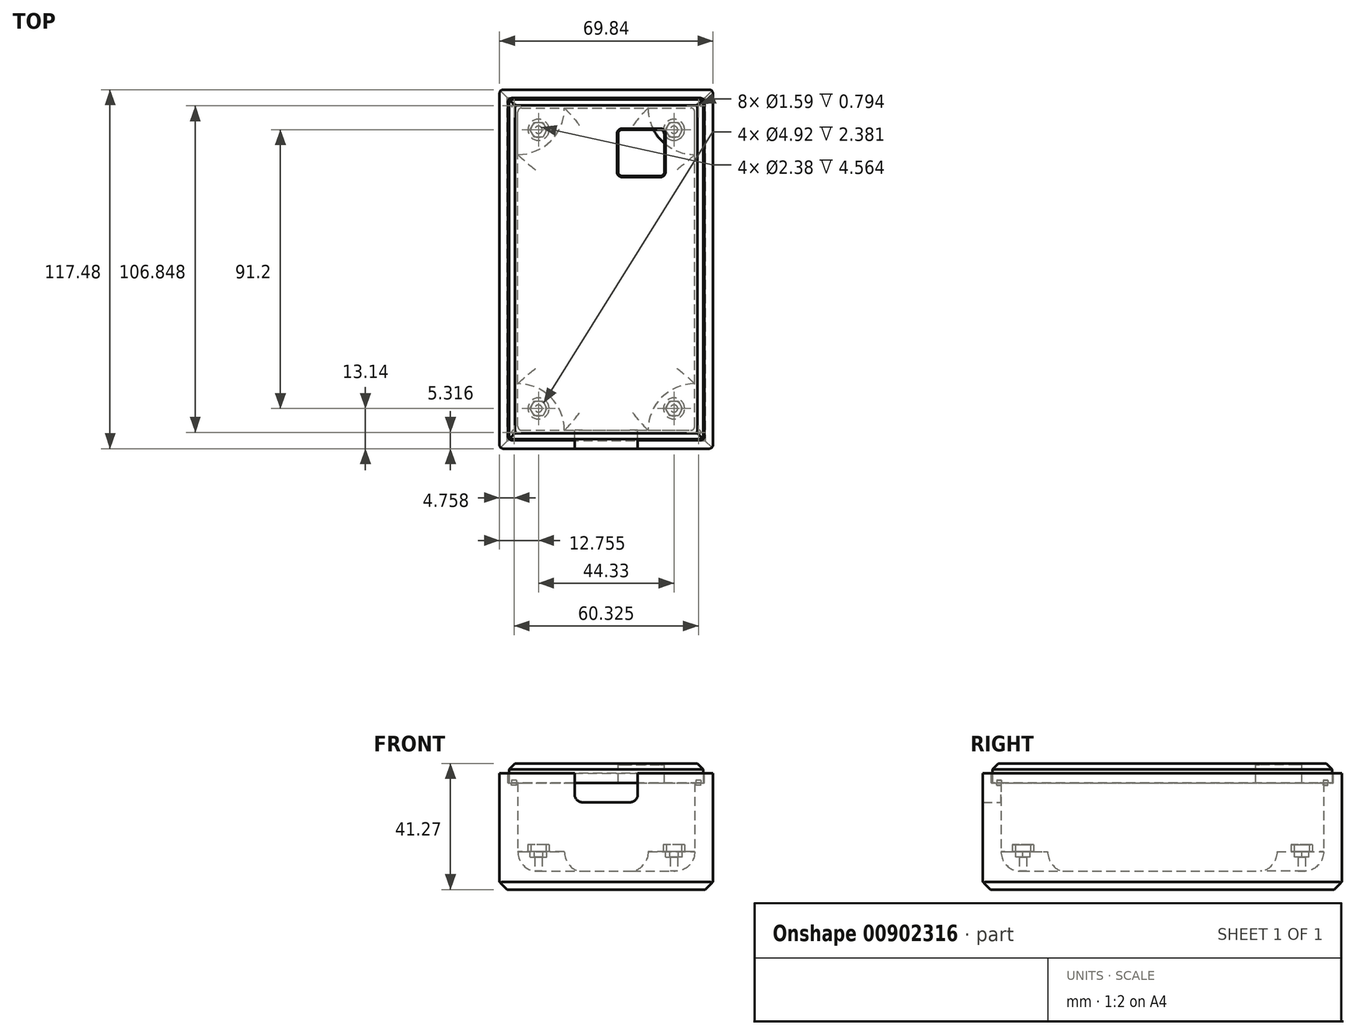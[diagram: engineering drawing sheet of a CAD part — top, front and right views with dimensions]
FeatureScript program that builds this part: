
annotation { "Feature Type Name" : "Feature", "Feature Type Description" : "" }
export const myFeature = defineFeature(function(context is Context, id is Id, definition is map)
    precondition{}
    {
        {
            var Q0;
            Q0=qCreatedBy(makeId("Top.planeOp"),FACE);
            var sketch = newSketch(context, id + "F0", { "sketchPlane" : qUnion([Q0])});
            skLineSegment(sketch, "E0.bottom", {"start": v(-34.92, -58.74) * mm, "end": v(34.93, -58.74) * mm});
            skLineSegment(sketch, "E0.top", {"start": v(-34.93, 58.74) * mm, "end": v(34.92, 58.74) * mm});
            skLineSegment(sketch, "E0.left", {"start": v(-34.92, -58.74) * mm, "end": v(-34.93, 58.74) * mm});
            skLineSegment(sketch, "E0.right", {"start": v(34.93, -58.74) * mm, "end": v(34.92, 58.74) * mm});
            skPoint(sketch, "E0.middle", {"position": v(0, 0) * mm});
            skSolve(sketch);
        }
        {
            var Q0;
            Q0=makeQuery(id+"F0.imprint","IMPRINT",FACE,{"disambiguationData":[TD([[makeQuery(id+"F0.imprint","IMPRINT",EDGE,{"derivedFrom":sQuery(id+"F0.wireOp",EDGE,"E0.bottom")}),1.0]])]});
            extrude(context, id + "F1", {"entities" : qUnion([Q0]), "depth" : 38.1 * mm, "offsetDistance" : 25.4 * mm});
        }
        {
            var Q0;
            Q0=makeQuery(id+"F1.opExtrude","CAP_FACE",FACE,{"disambiguationData":[OSD([sQuery(id+"F0.wireOp",EDGE,"E0.bottom"),sQuery(id+"F0.wireOp",EDGE,"E0.top"),sQuery(id+"F0.wireOp",EDGE,"E0.left"),sQuery(id+"F0.wireOp",EDGE,"E0.right")])],"isStart":false});
            shell(context, id + "F2", {"entities" : qUnion([Q0]), "thickness" : 6 * mm});
        }
        {
            var Q0;
            Q0=makeQuery(id+"F1.opExtrude","CAP_FACE",FACE,{"disambiguationData":[OSD([sQuery(id+"F0.wireOp",EDGE,"E0.bottom"),sQuery(id+"F0.wireOp",EDGE,"E0.top"),sQuery(id+"F0.wireOp",EDGE,"E0.left"),sQuery(id+"F0.wireOp",EDGE,"E0.right")])],"isStart":false});
            cPlane(context, id + "F3", {"entities" : qUnion([Q0]), "cplaneType" : CPlaneType.OFFSET, "offset" : 0 * mm, "oppositeDirection" : true, "width" : 152.4 * mm, "height" : 152.4 * mm});
        }
        {
            var Q0;
            Q0=qCreatedBy(id+"F3.planeOp",FACE);
            var sketch = newSketch(context, id + "F4", { "sketchPlane" : qUnion([Q0])});
            skLineSegment(sketch, "E1.bottom", {"start": v(32.15, -55.96) * mm, "end": v(-32.15, -55.96) * mm});
            skLineSegment(sketch, "E1.top", {"start": v(32.15, 55.96) * mm, "end": v(-32.15, 55.96) * mm});
            skLineSegment(sketch, "E1.left", {"start": v(32.15, -55.96) * mm, "end": v(32.15, 55.96) * mm});
            skLineSegment(sketch, "E1.right", {"start": v(-32.15, -55.96) * mm, "end": v(-32.15, 55.96) * mm});
            skPoint(sketch, "E1.middle", {"position": v(0, 0) * mm});
            skSolve(sketch);
        }
        {
            var Q0;
            Q0 = qSketchRegion(id + "F4", true);
            extrude(context, id + "F5", {"entities" : qUnion([Q0]), "operationType" : NewBodyOperationType.REMOVE, "oppositeDirection" : true, "depth" : 3.17 * mm, "offsetDistance" : 25.4 * mm});
        }
        {
            var Q0;
            Q0=makeQuery(id+"F2.opShell","OFFSET_FACE",FACE,{"disambiguationData":[OSD([sQuery(id+"F0.wireOp",EDGE,"E0.bottom"),sQuery(id+"F0.wireOp",EDGE,"E0.top"),sQuery(id+"F0.wireOp",EDGE,"E0.left"),sQuery(id+"F0.wireOp",EDGE,"E0.right")])]});
            var sketch = newSketch(context, id + "F6", { "sketchPlane" : qUnion([Q0])});
            skArc(sketch, "E2", {"start": v(-13.69, -52.74) * mm, "mid": v(-18.15, -41.96) * mm, "end": v(-28.93, -37.5) * mm});
            skArc(sketch, "E3", {"start": v(-28.93, 37.5) * mm, "mid": v(-18.15, 41.96) * mm, "end": v(-13.69, 52.74) * mm});
            skArc(sketch, "E4", {"start": v(28.93, -37.5) * mm, "mid": v(18.15, -41.96) * mm, "end": v(13.69, -52.74) * mm});
            skArc(sketch, "E5", {"start": v(13.68, 52.74) * mm, "mid": v(18.15, 41.96) * mm, "end": v(28.92, 37.5) * mm});
            skLineSegment(sketch, "E6", {"start": v(-28.93, 0) * mm, "end": v(28.93, 0) * mm, "construction": true});
            skLineSegment(sketch, "E7", {"start": v(0, -52.74) * mm, "end": v(0, 52.74) * mm, "construction": true});
            skCircle(sketch, "E8", {"center": v(-22.16, -45.6) * mm, "radius": 1.2 * mm});
            skCircle(sketch, "E9", {"center": v(22.16, -45.6) * mm, "radius": 1.2 * mm});
            skCircle(sketch, "E10", {"center": v(22.16, 45.6) * mm, "radius": 1.2 * mm});
            skCircle(sketch, "E11", {"center": v(-22.16, 45.6) * mm, "radius": 1.2 * mm});
            skLineSegment(sketch, "E12", {"start": v(-28.93, -37.5) * mm, "end": v(-28.93, -52.74) * mm});
            skLineSegment(sketch, "E13", {"start": v(-13.69, -52.74) * mm, "end": v(-28.93, -52.74) * mm});
            skLineSegment(sketch, "E14", {"start": v(13.69, -52.74) * mm, "end": v(28.93, -52.74) * mm});
            skLineSegment(sketch, "E15", {"start": v(28.93, -52.74) * mm, "end": v(28.93, -37.5) * mm});
            skLineSegment(sketch, "E16", {"start": v(-28.93, 37.5) * mm, "end": v(-28.93, 52.74) * mm});
            skLineSegment(sketch, "E17", {"start": v(-28.93, 52.74) * mm, "end": v(-13.69, 52.74) * mm});
            skLineSegment(sketch, "E18", {"start": v(13.68, 52.74) * mm, "end": v(28.92, 52.74) * mm});
            skLineSegment(sketch, "E19", {"start": v(28.92, 37.5) * mm, "end": v(28.92, 52.74) * mm});
            skSolve(sketch);
        }
        {
            var Q0;
            Q0 = qSketchRegion(id + "F6", true);
            extrude(context, id + "F7", {"entities" : qUnion([Q0]), "operationType" : NewBodyOperationType.ADD, "depth" : 6.35 * mm, "offsetDistance" : 25.4 * mm});
        }
        {
            var Q0;
            Q0=makeQuery(id+"F7.opExtrude","CAP_FACE",FACE,{"disambiguationData":[OSD([sQuery(id+"F6.wireOp",EDGE,"E2"),sQuery(id+"F6.wireOp",EDGE,"E8"),sQuery(id+"F6.wireOp",EDGE,"E12"),sQuery(id+"F6.wireOp",EDGE,"E13")])],"isStart":false});
            cPlane(context, id + "F8", {"entities" : qUnion([Q0]), "cplaneType" : CPlaneType.OFFSET, "offset" : 0 * mm, "width" : 152.4 * mm, "height" : 152.4 * mm});
        }
        {
            var Q0;
            Q0=qCreatedBy(id+"F8.planeOp",FACE);
            var sketch = newSketch(context, id + "F9", { "sketchPlane" : qUnion([Q0])});
            skCircle(sketch, "E20.cCircle", {"center": v(-22.16, -45.6) * mm, "radius": 2.75 * mm, "construction": true});
            skLineSegment(sketch, "E20.0", {"start": v(-19.41, -45.6) * mm, "end": v(-20.79, -47.98) * mm});
            skLineSegment(sketch, "E20.1", {"start": v(-20.79, -47.98) * mm, "end": v(-23.54, -47.98) * mm});
            skLineSegment(sketch, "E20.2", {"start": v(-23.54, -47.98) * mm, "end": v(-24.91, -45.6) * mm});
            skLineSegment(sketch, "E20.3", {"start": v(-24.91, -45.6) * mm, "end": v(-23.54, -43.22) * mm});
            skLineSegment(sketch, "E20.4", {"start": v(-23.54, -43.22) * mm, "end": v(-20.79, -43.22) * mm});
            skLineSegment(sketch, "E20.5", {"start": v(-20.79, -43.22) * mm, "end": v(-19.41, -45.6) * mm});
            skCircle(sketch, "E21.cCircle", {"center": v(22.16, -45.6) * mm, "radius": 2.75 * mm, "construction": true});
            skLineSegment(sketch, "E21.0", {"start": v(23.54, -47.98) * mm, "end": v(20.79, -47.98) * mm});
            skLineSegment(sketch, "E21.1", {"start": v(20.79, -47.98) * mm, "end": v(19.42, -45.6) * mm});
            skLineSegment(sketch, "E21.2", {"start": v(19.41, -45.6) * mm, "end": v(20.8, -43.22) * mm});
            skLineSegment(sketch, "E21.3", {"start": v(20.8, -43.22) * mm, "end": v(23.54, -43.22) * mm});
            skLineSegment(sketch, "E21.4", {"start": v(23.54, -43.22) * mm, "end": v(24.91, -45.6) * mm});
            skLineSegment(sketch, "E21.5", {"start": v(24.92, -45.6) * mm, "end": v(23.54, -47.98) * mm});
            skLineSegment(sketch, "E22", {"start": v(-23.36, -45.6) * mm, "end": v(-20.97, -45.6) * mm, "construction": true});
            skLineSegment(sketch, "E23", {"start": v(22.16, -46.8) * mm, "end": v(22.16, -44.4) * mm, "construction": true});
            skLineSegment(sketch, "E24", {"start": v(22.16, 44.4) * mm, "end": v(22.16, 46.8) * mm, "construction": true});
            skLineSegment(sketch, "E25", {"start": v(-23.36, 45.6) * mm, "end": v(-20.97, 45.6) * mm, "construction": true});
            skCircle(sketch, "E26.cCircle", {"center": v(-22.16, 45.6) * mm, "radius": 2.75 * mm, "construction": true});
            skLineSegment(sketch, "E26.0", {"start": v(-20.79, 47.98) * mm, "end": v(-19.41, 45.6) * mm});
            skLineSegment(sketch, "E26.1", {"start": v(-19.41, 45.6) * mm, "end": v(-20.79, 43.22) * mm});
            skLineSegment(sketch, "E26.2", {"start": v(-20.79, 43.22) * mm, "end": v(-23.54, 43.22) * mm});
            skLineSegment(sketch, "E26.3", {"start": v(-23.54, 43.22) * mm, "end": v(-24.91, 45.6) * mm});
            skLineSegment(sketch, "E26.4", {"start": v(-24.91, 45.6) * mm, "end": v(-23.54, 47.98) * mm});
            skLineSegment(sketch, "E26.5", {"start": v(-23.54, 47.98) * mm, "end": v(-20.79, 47.98) * mm});
            skCircle(sketch, "E27.cCircle", {"center": v(22.16, 45.6) * mm, "radius": 2.75 * mm, "construction": true});
            skLineSegment(sketch, "E27.0", {"start": v(24.91, 45.6) * mm, "end": v(23.54, 43.22) * mm});
            skLineSegment(sketch, "E27.1", {"start": v(23.54, 43.22) * mm, "end": v(20.79, 43.22) * mm});
            skLineSegment(sketch, "E27.2", {"start": v(20.79, 43.22) * mm, "end": v(19.41, 45.6) * mm});
            skLineSegment(sketch, "E27.3", {"start": v(19.41, 45.6) * mm, "end": v(20.79, 47.98) * mm});
            skLineSegment(sketch, "E27.4", {"start": v(20.79, 47.98) * mm, "end": v(23.54, 47.98) * mm});
            skLineSegment(sketch, "E27.5", {"start": v(23.54, 47.98) * mm, "end": v(24.91, 45.6) * mm});
            skSolve(sketch);
        }
        {
            var Q0;
            Q0 = qSketchRegion(id + "F9", true);
            extrude(context, id + "F10", {"entities" : qUnion([Q0]), "operationType" : NewBodyOperationType.REMOVE, "oppositeDirection" : true, "depth" : 1.79 * mm, "offsetDistance" : 25.4 * mm});
        }
        {
            var Q0;
            Q0=makeQuery(id+"F1.opExtrude","CAP_FACE",FACE,{"disambiguationData":[OSD([sQuery(id+"F0.wireOp",EDGE,"E0.bottom"),sQuery(id+"F0.wireOp",EDGE,"E0.top"),sQuery(id+"F0.wireOp",EDGE,"E0.left"),sQuery(id+"F0.wireOp",EDGE,"E0.right")])],"isStart":false});
            var sketch = newSketch(context, id + "F11", { "sketchPlane" : qUnion([Q0])});
            skLineSegment(sketch, "E28.bottom", {"start": v(-10.32, -58.74) * mm, "end": v(10.32, -58.74) * mm});
            skLineSegment(sketch, "E28.top", {"start": v(-10.32, -52.22) * mm, "end": v(10.32, -52.22) * mm});
            skLineSegment(sketch, "E28.left", {"start": v(-10.32, -58.74) * mm, "end": v(-10.32, -52.22) * mm});
            skLineSegment(sketch, "E28.right", {"start": v(10.32, -58.74) * mm, "end": v(10.32, -52.22) * mm});
            skLineSegment(sketch, "E29", {"start": v(0, -58.74) * mm, "end": v(0, 58.74) * mm, "construction": true});
            skSolve(sketch);
        }
        {
            var Q0;
            Q0 = qSketchRegion(id + "F11", true);
            extrude(context, id + "F12", {"entities" : qUnion([Q0]), "operationType" : NewBodyOperationType.REMOVE, "oppositeDirection" : true, "depth" : 9.52 * mm, "offsetDistance" : 25.4 * mm});
        }
        {
            var Q0;
            {var subQ0=sQuery(id+"F0.wireOp",EDGE,"E0.right");var subQ1=sQuery(id+"F0.wireOp",EDGE,"E0.left");var subQ2=sQuery(id+"F0.wireOp",EDGE,"E0.top");var subQ3=sQuery(id+"F0.wireOp",EDGE,"E0.bottom");Q0=makeQuery(id+"F7.boolean.opBoolean","SPLIT",FACE,{"disambiguationData":[TD([makeQuery(id+"F2.opShell","OFFSET_FACE",FACE,{"disambiguationData":[OSD([subQ3])]})])],"derivedFrom":makeQuery(id+"F2.opShell","OFFSET_FACE",FACE,{"disambiguationData":[OSD([subQ3,subQ2,subQ1,subQ0])]})});}
            fillet(context, id + "F13", {"entities" : qUnion([Q0]), "radius" : 6.35 * mm, "tangentPropagation" : true, "allowEdgeOverflow" : false});
        }
        {
            var Q0;
            Q0=makeQuery(id+"F2.opShell","OFFSET_EDGE",EDGE,{"disambiguationData":[OSD([sQuery(id+"F0.wireOp",EDGE,"E0.bottom"),sQuery(id+"F0.wireOp",EDGE,"E0.left")])]});
            var Q1;
            Q1=makeQuery(id+"F2.opShell","OFFSET_EDGE",EDGE,{"disambiguationData":[OSD([sQuery(id+"F0.wireOp",EDGE,"E0.top"),sQuery(id+"F0.wireOp",EDGE,"E0.left")])]});
            var Q2;
            Q2=makeQuery(id+"F2.opShell","OFFSET_EDGE",EDGE,{"disambiguationData":[OSD([sQuery(id+"F0.wireOp",EDGE,"E0.bottom"),sQuery(id+"F0.wireOp",EDGE,"E0.right")])]});
            var Q3;
            Q3=makeQuery(id+"F2.opShell","OFFSET_EDGE",EDGE,{"disambiguationData":[OSD([sQuery(id+"F0.wireOp",EDGE,"E0.top"),sQuery(id+"F0.wireOp",EDGE,"E0.right")])]});
            fillet(context, id + "F14", {"entities" : qUnion([Q0, Q1, Q2, Q3]), "radius" : 1.27 * mm, "tangentPropagation" : true, "allowEdgeOverflow" : false});
        }
        {
            var Q0;
            Q0=makeQuery(id+"F1.opExtrude","CAP_FACE",FACE,{"disambiguationData":[OSD([sQuery(id+"F0.wireOp",EDGE,"E0.bottom"),sQuery(id+"F0.wireOp",EDGE,"E0.top"),sQuery(id+"F0.wireOp",EDGE,"E0.left"),sQuery(id+"F0.wireOp",EDGE,"E0.right")])],"isStart":true});
            chamfer(context, id + "F15", {"entities" : qUnion([Q0]), "width" : 2.54 * mm, "tangentPropagation" : true});
        }
        {
            var Q0;
            Q0=makeQuery(id+"F1.opExtrude","SWEPT_EDGE",EDGE,{"disambiguationData":[OSD([sQuery(id+"F0.wireOp",EDGE,"E0.bottom"),sQuery(id+"F0.wireOp",EDGE,"E0.right")])]});
            var Q1;
            Q1=makeQuery(id+"F1.opExtrude","SWEPT_EDGE",EDGE,{"disambiguationData":[OSD([sQuery(id+"F0.wireOp",EDGE,"E0.bottom"),sQuery(id+"F0.wireOp",EDGE,"E0.left")])]});
            var Q2;
            Q2=makeQuery(id+"F1.opExtrude","SWEPT_EDGE",EDGE,{"disambiguationData":[OSD([sQuery(id+"F0.wireOp",EDGE,"E0.top"),sQuery(id+"F0.wireOp",EDGE,"E0.left")])]});
            var Q3;
            Q3=makeQuery(id+"F1.opExtrude","SWEPT_EDGE",EDGE,{"disambiguationData":[OSD([sQuery(id+"F0.wireOp",EDGE,"E0.top"),sQuery(id+"F0.wireOp",EDGE,"E0.right")])]});
            fillet(context, id + "F16", {"entities" : qUnion([Q0, Q1, Q2, Q3]), "radius" : 1.27 * mm, "tangentPropagation" : true, "allowEdgeOverflow" : false});
        }
        {
            var Q0;
            Q0=makeQuery(id+"F12.boolean.opBoolean","COPY",EDGE,{"derivedFrom":makeQuery(id+"F12.opExtrude","CAP_EDGE",EDGE,{"disambiguationData":[OSD([sQuery(id+"F11.wireOp",EDGE,"E28.right")])],"isStart":false})});
            var Q1;
            Q1=makeQuery(id+"F12.boolean.opBoolean","COPY",EDGE,{"derivedFrom":makeQuery(id+"F12.opExtrude","CAP_EDGE",EDGE,{"disambiguationData":[OSD([sQuery(id+"F11.wireOp",EDGE,"E28.left")])],"isStart":false})});
            fillet(context, id + "F17", {"entities" : qUnion([Q0, Q1]), "radius" : 2.54 * mm, "tangentPropagation" : true, "allowEdgeOverflow" : false});
        }
        {
            var Q0;
            Q0=makeQuery(id+"F5.boolean.opBoolean","COPY",EDGE,{"derivedFrom":makeQuery(id+"F5.opExtrude","SWEPT_EDGE",EDGE,{"disambiguationData":[OSD([sQuery(id+"F4.wireOp",EDGE,"E1.bottom"),sQuery(id+"F4.wireOp",EDGE,"E1.left")])]})});
            var Q1;
            Q1=makeQuery(id+"F5.boolean.opBoolean","COPY",EDGE,{"derivedFrom":makeQuery(id+"F5.opExtrude","SWEPT_EDGE",EDGE,{"disambiguationData":[OSD([sQuery(id+"F4.wireOp",EDGE,"E1.top"),sQuery(id+"F4.wireOp",EDGE,"E1.left")])]})});
            var Q2;
            Q2=makeQuery(id+"F5.boolean.opBoolean","COPY",EDGE,{"derivedFrom":makeQuery(id+"F5.opExtrude","SWEPT_EDGE",EDGE,{"disambiguationData":[OSD([sQuery(id+"F4.wireOp",EDGE,"E1.top"),sQuery(id+"F4.wireOp",EDGE,"E1.right")])]})});
            var Q3;
            Q3=makeQuery(id+"F5.boolean.opBoolean","COPY",EDGE,{"derivedFrom":makeQuery(id+"F5.opExtrude","SWEPT_EDGE",EDGE,{"disambiguationData":[OSD([sQuery(id+"F4.wireOp",EDGE,"E1.bottom"),sQuery(id+"F4.wireOp",EDGE,"E1.right")])]})});
            fillet(context, id + "F18", {"entities" : qUnion([Q0, Q1, Q2, Q3]), "radius" : 1.27 * mm, "tangentPropagation" : true, "allowEdgeOverflow" : false});
        }
        {
            var Q0;
            Q0=makeQuery(id+"F5.boolean.opBoolean","COPY",FACE,{"derivedFrom":makeQuery(id+"F5.opExtrude","CAP_FACE",FACE,{"disambiguationData":[OSD([sQuery(id+"F4.wireOp",EDGE,"E1.bottom"),sQuery(id+"F4.wireOp",EDGE,"E1.top"),sQuery(id+"F4.wireOp",EDGE,"E1.left"),sQuery(id+"F4.wireOp",EDGE,"E1.right")])],"isStart":false})});
            var sketch = newSketch(context, id + "F19", { "sketchPlane" : qUnion([Q0])});
            skLineSegment(sketch, "E30.bottom", {"start": v(-31.75, 55.56) * mm, "end": v(31.75, 55.56) * mm});
            skLineSegment(sketch, "E30.top", {"start": v(-31.75, -55.56) * mm, "end": v(31.75, -55.56) * mm});
            skLineSegment(sketch, "E30.left", {"start": v(31.75, 55.56) * mm, "end": v(31.75, -55.56) * mm});
            skLineSegment(sketch, "E30.right", {"start": v(-31.75, 55.56) * mm, "end": v(-31.75, -55.56) * mm});
            skPoint(sketch, "E30.middle", {"position": v(0, 0) * mm});
            skSolve(sketch);
        }
        {
            var Q0;
            Q0 = qSketchRegion(id + "F19", true);
            extrude(context, id + "F20", {"entities" : qUnion([Q0]), "depth" : 6.35 * mm, "offsetDistance" : 25.4 * mm});
        }
        {
            var Q0;
            Q0=makeQuery(id+"F20.opExtrude","CAP_FACE",FACE,{"disambiguationData":[OSD([sQuery(id+"F19.wireOp",EDGE,"E30.bottom"),sQuery(id+"F19.wireOp",EDGE,"E30.top"),sQuery(id+"F19.wireOp",EDGE,"E30.left"),sQuery(id+"F19.wireOp",EDGE,"E30.right")])],"isStart":false});
            chamfer(context, id + "F21", {"entities" : qUnion([Q0]), "width" : 1.9 * mm, "tangentPropagation" : true});
        }
        {
            var Q0;
            Q0=makeQuery(id+"F1.opExtrude","CAP_FACE",FACE,{"disambiguationData":[OSD([sQuery(id+"F0.wireOp",EDGE,"E0.bottom"),sQuery(id+"F0.wireOp",EDGE,"E0.top"),sQuery(id+"F0.wireOp",EDGE,"E0.left"),sQuery(id+"F0.wireOp",EDGE,"E0.right")])],"isStart":false});
            cPlane(context, id + "F22", {"entities" : qUnion([Q0]), "cplaneType" : CPlaneType.OFFSET, "offset" : 6.35 * mm, "width" : 152.4 * mm, "height" : 152.4 * mm});
        }
        {
            var Q0;
            Q0=qCreatedBy(id+"F22.planeOp",FACE);
            var sketch = newSketch(context, id + "F23", { "sketchPlane" : qUnion([Q0])});
            skLineSegment(sketch, "E31.bottom", {"start": v(3.9, 30.52) * mm, "end": v(18.99, 30.52) * mm});
            skLineSegment(sketch, "E31.top", {"start": v(3.9, 45.6) * mm, "end": v(18.99, 45.6) * mm});
            skLineSegment(sketch, "E31.left", {"start": v(3.9, 30.52) * mm, "end": v(3.9, 45.6) * mm});
            skLineSegment(sketch, "E31.right", {"start": v(18.99, 30.52) * mm, "end": v(18.99, 45.6) * mm});
            skPoint(sketch, "E31.middle", {"position": v(11.45, 38.06) * mm});
            skLineSegment(sketch, "E32", {"start": v(20.79, 47.98) * mm, "end": v(23.54, 43.22) * mm, "construction": true});
            skLineSegment(sketch, "E33", {"start": v(23.54, 47.98) * mm, "end": v(20.79, 43.22) * mm, "construction": true});
            skPoint(sketch, "E34", {"position": v(22.16, 45.6) * mm});
            skSolve(sketch);
        }
        {
            var Q0;
            Q0 = qSketchRegion(id + "F23", true);
            extrude(context, id + "F24", {"entities" : qUnion([Q0]), "operationType" : NewBodyOperationType.REMOVE, "oppositeDirection" : true, "depth" : 25.4 * mm, "offsetDistance" : 25.4 * mm});
        }
        {
            var Q0;
            Q0=makeQuery(id+"F24.boolean.opBoolean","COPY",EDGE,{"derivedFrom":makeQuery(id+"F24.opExtrude","SWEPT_EDGE",EDGE,{"disambiguationData":[OSD([sQuery(id+"F23.wireOp",EDGE,"E31.top"),sQuery(id+"F23.wireOp",EDGE,"E31.right")])]})});
            var Q1;
            Q1=makeQuery(id+"F24.boolean.opBoolean","COPY",EDGE,{"derivedFrom":makeQuery(id+"F24.opExtrude","SWEPT_EDGE",EDGE,{"disambiguationData":[OSD([sQuery(id+"F23.wireOp",EDGE,"E31.top"),sQuery(id+"F23.wireOp",EDGE,"E31.left")])]})});
            var Q2;
            Q2=makeQuery(id+"F24.boolean.opBoolean","COPY",EDGE,{"derivedFrom":makeQuery(id+"F24.opExtrude","SWEPT_EDGE",EDGE,{"disambiguationData":[OSD([sQuery(id+"F23.wireOp",EDGE,"E31.bottom"),sQuery(id+"F23.wireOp",EDGE,"E31.left")])]})});
            var Q3;
            Q3=makeQuery(id+"F24.boolean.opBoolean","COPY",EDGE,{"derivedFrom":makeQuery(id+"F24.opExtrude","SWEPT_EDGE",EDGE,{"disambiguationData":[OSD([sQuery(id+"F23.wireOp",EDGE,"E31.bottom"),sQuery(id+"F23.wireOp",EDGE,"E31.right")])]})});
            fillet(context, id + "F25", {"entities" : qUnion([Q0, Q1, Q2, Q3]), "radius" : 1.27 * mm, "tangentPropagation" : true, "allowEdgeOverflow" : false});
        }
        {
            var Q0;
            Q0=makeQuery(id+"F5.boolean.opBoolean","COPY",FACE,{"derivedFrom":makeQuery(id+"F5.opExtrude","CAP_FACE",FACE,{"disambiguationData":[OSD([sQuery(id+"F4.wireOp",EDGE,"E1.bottom"),sQuery(id+"F4.wireOp",EDGE,"E1.top"),sQuery(id+"F4.wireOp",EDGE,"E1.left"),sQuery(id+"F4.wireOp",EDGE,"E1.right")])],"isStart":false})});
            var sketch = newSketch(context, id + "F26", { "sketchPlane" : qUnion([Q0])});
            skCircle(sketch, "E35", {"center": v(30.16, 53.42) * mm, "radius": 0.8 * mm});
            skCircle(sketch, "E36", {"center": v(30.16, -53.42) * mm, "radius": 0.8 * mm});
            skCircle(sketch, "E37", {"center": v(-30.16, -53.42) * mm, "radius": 0.8 * mm});
            skCircle(sketch, "E38", {"center": v(-30.16, 53.42) * mm, "radius": 0.8 * mm});
            skLineSegment(sketch, "E39", {"start": v(-30.88, -54.69) * mm, "end": v(30.88, 54.69) * mm, "construction": true});
            skLineSegment(sketch, "E40", {"start": v(-30.88, 54.69) * mm, "end": v(30.88, -54.69) * mm, "construction": true});
            skLineSegment(sketch, "E41", {"start": v(0, 52.74) * mm, "end": v(0, 0) * mm, "construction": true});
            skLineSegment(sketch, "E42", {"start": v(-28.93, 0) * mm, "end": v(28.93, 0) * mm, "construction": true});
            skSolve(sketch);
        }
        {
            var Q0;
            Q0 = qSketchRegion(id + "F26", true);
            extrude(context, id + "F27", {"entities" : qUnion([Q0]), "operationType" : NewBodyOperationType.REMOVE, "oppositeDirection" : true, "depth" : 0.8 * mm, "offsetDistance" : 25.4 * mm});
        }
        {
            var Q0;
            Q0 = qSketchRegion(id + "F26", true);
            extrude(context, id + "F28", {"entities" : qUnion([Q0]), "operationType" : NewBodyOperationType.REMOVE, "depth" : 0.8 * mm, "offsetDistance" : 25.4 * mm});
        }
        {
            var Q0;
            Q0=makeQuery(id+"F24.boolean.opBoolean","INTERSECT",EDGE,{"derivedFrom":[makeQuery(id+"F20.opExtrude","CAP_FACE",FACE,{"disambiguationData":[OSD([sQuery(id+"F19.wireOp",EDGE,"E30.bottom"),sQuery(id+"F19.wireOp",EDGE,"E30.top"),sQuery(id+"F19.wireOp",EDGE,"E30.left"),sQuery(id+"F19.wireOp",EDGE,"E30.right")])],"isStart":false}),makeQuery(id+"F24.opExtrude","SWEPT_FACE",FACE,{"disambiguationData":[OSD([sQuery(id+"F23.wireOp",EDGE,"E31.top")])]})]});
            chamfer(context, id + "F29", {"entities" : qUnion([Q0]), "width" : .4 * mm, "tangentPropagation" : true});
        }
        {
            var Q0;
            Q0=makeQuery(id+"F7.opExtrude","CAP_FACE",FACE,{"disambiguationData":[OSD([sQuery(id+"F6.wireOp",EDGE,"E3"),sQuery(id+"F6.wireOp",EDGE,"E11"),sQuery(id+"F6.wireOp",EDGE,"E16"),sQuery(id+"F6.wireOp",EDGE,"E17")])],"isStart":false});
            var sketch = newSketch(context, id + "F30", { "sketchPlane" : qUnion([Q0])});
            skCircle(sketch, "E43", {"center": v(-22.16, 45.6) * mm, "radius": 2.46 * mm});
            skCircle(sketch, "E44", {"center": v(-22.16, 45.6) * mm, "radius": 3.46 * mm});
            skCircle(sketch, "E45", {"center": v(22.16, 45.6) * mm, "radius": 3.46 * mm});
            skCircle(sketch, "E46", {"center": v(22.16, 45.6) * mm, "radius": 2.46 * mm});
            skCircle(sketch, "E47", {"center": v(-22.16, -45.6) * mm, "radius": 2.46 * mm});
            skCircle(sketch, "E48", {"center": v(-22.16, -45.6) * mm, "radius": 3.46 * mm});
            skCircle(sketch, "E49", {"center": v(22.16, -45.6) * mm, "radius": 2.46 * mm});
            skCircle(sketch, "E50", {"center": v(22.16, -45.6) * mm, "radius": 3.46 * mm});
            skSolve(sketch);
        }
        {
            var Q0;
            Q0 = qSketchRegion(id + "F30", true);
            extrude(context, id + "F31", {"entities" : qUnion([Q0]), "depth" : 2.38 * mm, "offsetDistance" : 25.4 * mm});
        }
    });
